# Revit family: BE_33405_de_DE
name_source: partatom
category: Leuchten
units: mm (PartAtom-declared; Revit-internal decimal feet)

## family parameters
Basisbauteil = Fläche
Beim Laden mit Abzugskörper schneiden = Ja
Bemaßung runder Anschluss = Durchmesser verwenden
Gemeinsam genutzt = Nein
Lichtquelle = Ja
Raumberechnungspunkt = Ja
Teiletyp = Normal

## types (2) — shared parameters
AC/DC = AC/DC
Aktualisierung = 2022-05-18T04:00:07
BEGA_Dummy = Nein
BEGA_IES = Ja
BEGA_Intern = Ja
BEGA_Intern_Konstruktion = Ja
BEGA_Intern_an = Ja
BEGA_Intern_aus = Ja
Befestigungsabstand = 65 mm
Befestigungsbohrung = Ø 4,5 mm
Beschreibung = Wandleuchte
Beschreibung_Sonderanfertigung = Hier können Sie Informationen zur Sonderanfertigung eintragen.
CE_Konformität = ja
Datei für fotometrisches Netz = BE_33405K3.IES
Energieeffizienzklasse = LED A++ - A
Farbfilter = 16777215
Farbtemperatur = 3000 K
Farbtemperaturverschiebung bei Dämpfen der Lampe = <Keine Auswahl>
Farbwiedergabeindex = CRI > 80
Frequenz = 0/50-60 Hz
Gewicht = 0.95 kg
Hersteller = BEGA
LED_Modulbezeichnung = LED-0265/830
Lampe = LED 3.9 W
Lampenlichtstrom = 750 lm
Lastklassifizierung = Beleuchtung
Lebensdauerkriterien = L70B50 @ 25 °C = 200000 h
Leuchtenlichtstrom = 215 lm
Logo = BEGA_Logo.png
Material_02 = BEGA_Oberfläche_Silber_matt
Material_06 = BEGA_Oberfläche_Edelstahl_gebürstet
Material_09 = BEGA_Glas_klar
Material_11 = BEGA_Glas_opal
Material_15 = BEGA_Leuchtmedium_matt
Material_19 = BEGA_Dummy_matt
Neigungswinkel = 0.00°
Produktdatenblatt = https://cdn.bega.com
Scheinlast = 0 VA
Schutzart = IP 64
Schutzklasse = I
Sonderanfertigung = Nein
Spannung = 240 V
Typenbild = 33405.png
URL = https://www.bega.com
zero-valued in all types: Vorgabe-Ansicht

## per-type parameters (varying)
| type | Bestellnummer | M_A | M_G | Modell |
| BEGA_33405_Grafit_K3 | 33405K3 | Nein | Ja | 33405K3 |
| BEGA_33405_Silber_K3 | 33405AK3 | Ja | Nein | 33405AK3 |
